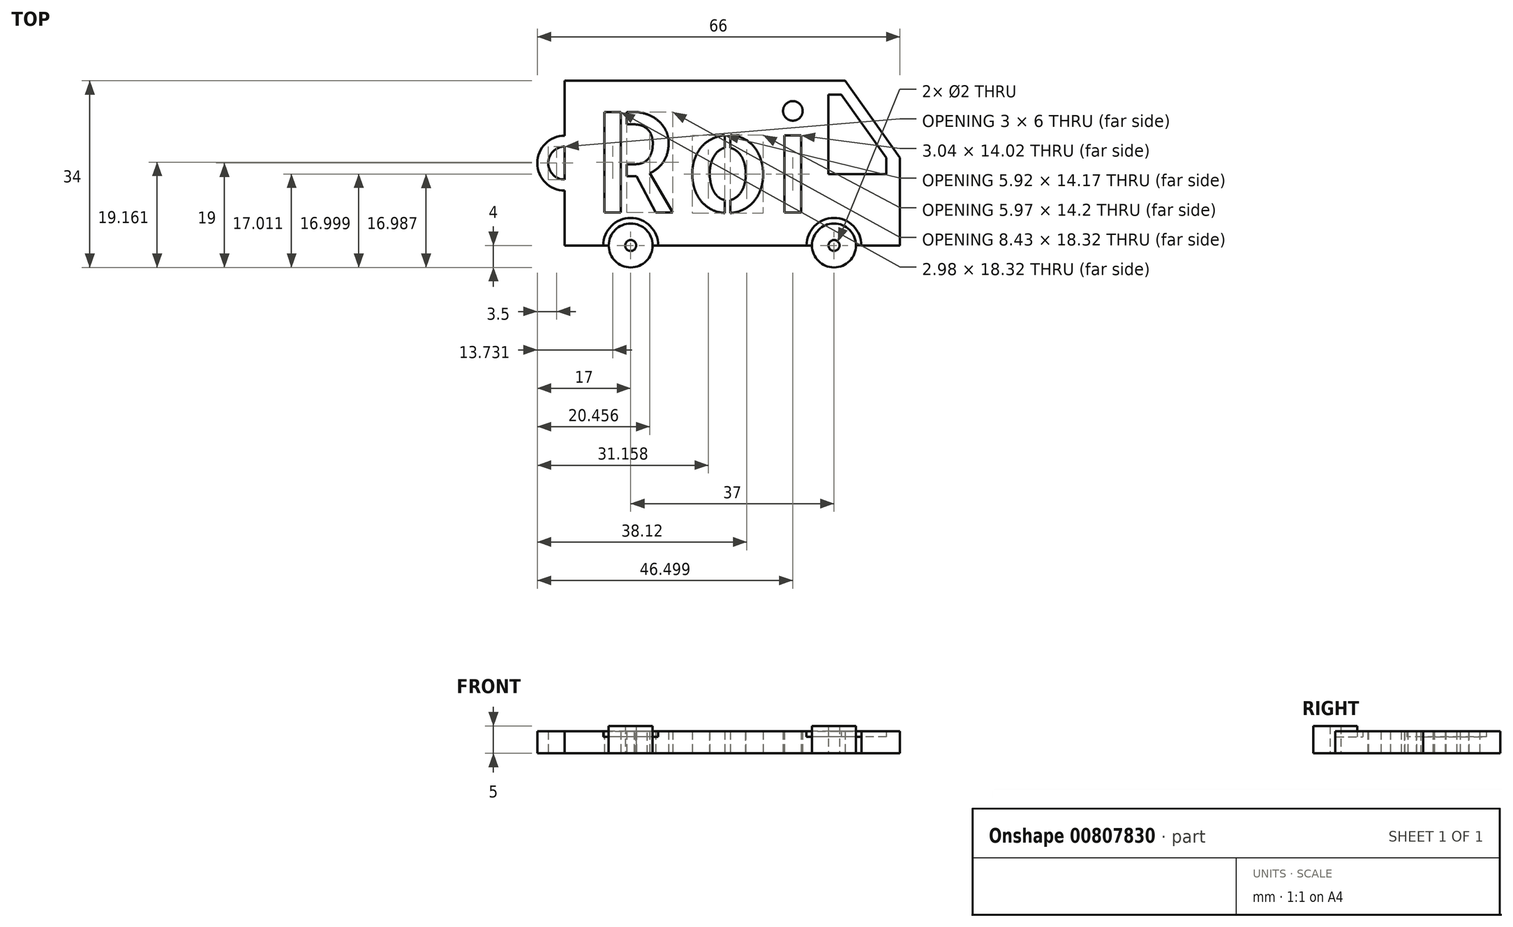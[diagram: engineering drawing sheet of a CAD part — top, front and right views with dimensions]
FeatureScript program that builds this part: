
annotation { "Feature Type Name" : "Feature", "Feature Type Description" : "" }
export const myFeature = defineFeature(function(context is Context, id is Id, definition is map)
    precondition{}
    {
        {
            var Q0;
            Q0=qCreatedBy(makeId("Top.planeOp"),FACE);
            var sketch = newSketch(context, id + "F0", { "sketchPlane" : qUnion([Q0])});
            skText(sketch, "E0", { "text": "Roi", "fontName": "AllertaStencil-Regular.ttf"});
            skPoint(sketch, "E1.centerSnap0", {"position": v(0, 9.17) * mm});
            skArc(sketch, "E2", {"start": v(12, -6) * mm, "mid": v(7, -1) * mm, "end": v(2, -6) * mm});
            skArc(sketch, "E3", {"start": v(49, -6) * mm, "mid": v(44, -1) * mm, "end": v(39, -6) * mm});
            skLineSegment(sketch, "E4", {"start": v(12, -6) * mm, "end": v(39, -6) * mm});
            skLineSegment(sketch, "E5", {"start": v(49, -6) * mm, "end": v(56, -6) * mm});
            skLineSegment(sketch, "E6", {"start": v(56, -6) * mm, "end": v(56, 10) * mm});
            skLineSegment(sketch, "E7", {"start": v(40, 24) * mm, "end": v(-5, 24) * mm});
            skLineSegment(sketch, "E8", {"start": v(-5, 24) * mm, "end": v(-5, 14) * mm});
            skLineSegment(sketch, "E9", {"start": v(-5, -6) * mm, "end": v(2, -6) * mm});
            skLineSegment(sketch, "E10", {"start": v(40, 24) * mm, "end": v(46, 24) * mm});
            skLineSegment(sketch, "E11", {"start": v(46, 24) * mm, "end": v(56, 10) * mm});
            skLineSegment(sketch, "E12", {"start": v(53.54, 10) * mm, "end": v(45.33, 21.5) * mm});
            skLineSegment(sketch, "E13", {"start": v(45.33, 21.5) * mm, "end": v(43, 21.5) * mm});
            skCircle(sketch, "E14", {"center": v(7, -6) * mm, "radius": 4 * mm});
            skCircle(sketch, "E15", {"center": v(44, -6) * mm, "radius": 4 * mm});
            skLineSegment(sketch, "E16", {"start": v(2, -6) * mm, "end": v(3, -6) * mm});
            skLineSegment(sketch, "E17", {"start": v(12, -6) * mm, "end": v(11, -6) * mm});
            skLineSegment(sketch, "E18", {"start": v(39, -6) * mm, "end": v(40, -6) * mm});
            skLineSegment(sketch, "E19", {"start": v(48, -5.95) * mm, "end": v(49, -6) * mm});
            skLineSegment(sketch, "E20", {"start": v(43, 21.5) * mm, "end": v(43, 7) * mm});
            skLineSegment(sketch, "E21", {"start": v(53.54, 10) * mm, "end": v(53.54, 7) * mm});
            skLineSegment(sketch, "E22", {"start": v(53.54, 7) * mm, "end": v(43, 7) * mm});
            skCircle(sketch, "E23", {"center": v(7, -6) * mm, "radius": 1 * mm});
            skCircle(sketch, "E24", {"center": v(44, -6) * mm, "radius": 1 * mm});
            skArc(sketch, "E25", {"start": v(-5, 14) * mm, "mid": v(-10, 9) * mm, "end": v(-5, 4) * mm});
            skArc(sketch, "E26", {"start": v(-5, 12) * mm, "mid": v(-8, 9) * mm, "end": v(-5, 6) * mm});
            skLineSegment(sketch, "E27.trimOffspring", {"start": v(-5, 12) * mm, "end": v(-5, 6) * mm});
            skLineSegment(sketch, "E28.trimOffspring", {"start": v(-5, 4) * mm, "end": v(-5, -6) * mm});
            const initialGuessF0  = {"E0": [0, 0, 1, 0, 0.01833]};
            skSetInitialGuess(sketch, initialGuessF0);
            skSolve(sketch);
        }
        {
            var Q0;
            Q0=makeQuery(id+"F0.imprint","IMPRINT",FACE,{"disambiguationData":[TD([[makeQuery(id+"F0.imprint","IMPRINT",EDGE,{"derivedFrom":sQuery(id+"F0.wireOp",EDGE,"E0.sketch_text.stroke-0")}),1.0]])]});
            extrude(context, id + "F1", {"entities" : qUnion([Q0]), "depth" : 4 * mm, "offsetDistance" : 25 * mm});
        }
        {
            var Q0;
            Q0=makeQuery(id+"F0.imprint","IMPRINT",FACE,{"disambiguationData":[TD([[makeQuery(id+"F0.imprint","IMPRINT",EDGE,{"derivedFrom":sQuery(id+"F0.wireOp",EDGE,"E0.sketch_text.stroke-0")}),1.0]])]});
            extrude(context, id + "F2", {"entities" : qUnion([Q0]), "operationType" : NewBodyOperationType.ADD, "depth" : 4 * mm, "offsetDistance" : 25 * mm});
        }
        {
            var Q0;
            Q0=makeQuery(id+"F0.imprint","IMPRINT",FACE,{"disambiguationData":[TD([[makeQuery(id+"F0.imprint","IMPRINT",EDGE,{"derivedFrom":sQuery(id+"F0.wireOp",EDGE,"E2")}),1.0]])]});
            var Q1;
            Q1=makeQuery(id+"F0.imprint","IMPRINT",FACE,{"disambiguationData":[TD([[makeQuery(id+"F0.imprint","IMPRINT",EDGE,{"derivedFrom":sQuery(id+"F0.wireOp",EDGE,"E3")}),1.0]])]});
            extrude(context, id + "F3", {"entities" : qUnion([Q0, Q1]), "operationType" : NewBodyOperationType.ADD, "depth" : 3 * mm, "offsetDistance" : 25 * mm});
        }
        {
            var Q0;
            {var subQ0=sQuery(id+"F0.wireOp",EDGE,"E14");var subQ1=makeQuery(id+"F0.imprint","INTERSECT",VERTEX,{"derivedFrom":[subQ0,sQuery(id+"F0.wireOp",EDGE,"E16")]});Q0=makeQuery(id+"F0.imprint","IMPRINT",FACE,{"disambiguationData":[TD([[makeQuery(id+"F0.imprint","IMPRINT",EDGE,{"disambiguationData":[TD([[subQ1,1.0]])],"derivedFrom":subQ0}),1.0]])]});}
            var Q1;
            {var subQ0=sQuery(id+"F0.wireOp",EDGE,"E15");var subQ1=makeQuery(id+"F0.imprint","INTERSECT",VERTEX,{"derivedFrom":[subQ0,sQuery(id+"F0.wireOp",EDGE,"E18")]});Q1=makeQuery(id+"F0.imprint","IMPRINT",FACE,{"disambiguationData":[TD([[makeQuery(id+"F0.imprint","IMPRINT",EDGE,{"disambiguationData":[TD([[subQ1,1.0]])],"derivedFrom":subQ0}),1.0]])]});}
            extrude(context, id + "F4", {"entities" : qUnion([Q0, Q1]), "operationType" : NewBodyOperationType.ADD, "depth" : 5 * mm, "offsetDistance" : 25 * mm});
        }
        {
            var Q0;
            Q0=makeQuery(id+"F0.imprint","IMPRINT",FACE,{"disambiguationData":[TD([[makeQuery(id+"F0.imprint","IMPRINT",EDGE,{"derivedFrom":sQuery(id+"F0.wireOp",EDGE,"E12")}),1.0]])]});
            extrude(context, id + "F5", {"entities" : qUnion([Q0]), "operationType" : NewBodyOperationType.ADD, "depth" : 3 * mm, "offsetDistance" : 25 * mm});
        }
    });
